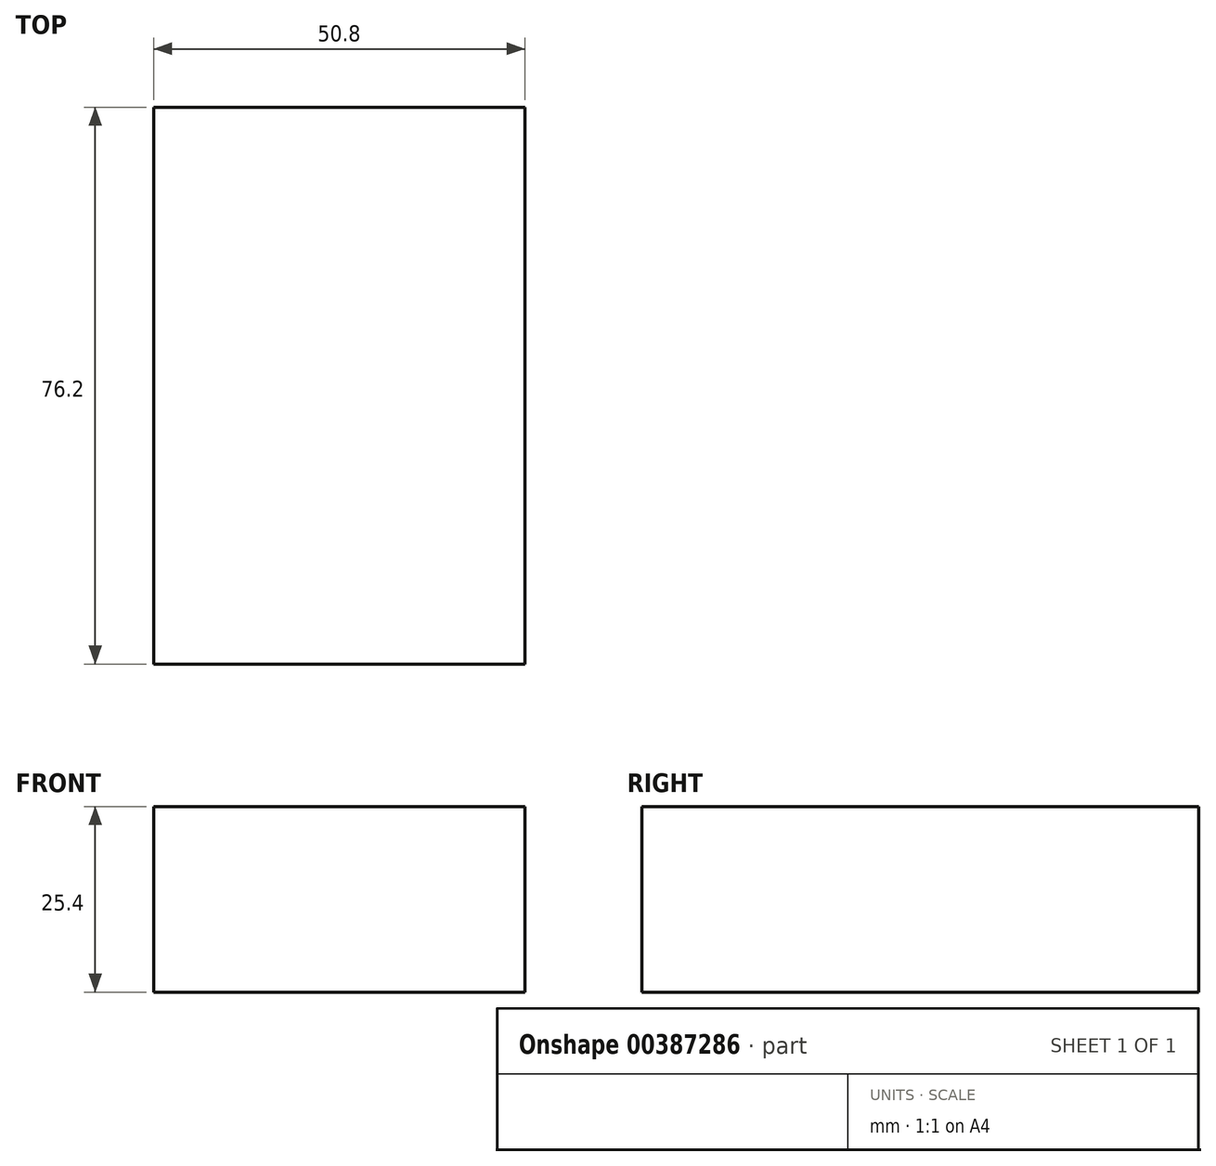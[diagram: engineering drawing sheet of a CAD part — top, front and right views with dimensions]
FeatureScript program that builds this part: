
annotation { "Feature Type Name" : "Feature", "Feature Type Description" : "" }
export const myFeature = defineFeature(function(context is Context, id is Id, definition is map)
    precondition{}
    {
        {
            var Q0;
            Q0=qCreatedBy(makeId("Top.planeOp"),FACE);
            var sketch = newSketch(context, id + "F0", { "sketchPlane" : qUnion([Q0])});
            skLineSegment(sketch, "E0.bottom", {"start": v(0, 0) * mm, "end": v(25.4, 0) * mm});
            skLineSegment(sketch, "E0.top", {"start": v(0, 25.4) * mm, "end": v(25.4, 25.4) * mm});
            skLineSegment(sketch, "E0.left", {"start": v(0, 0) * mm, "end": v(0, 25.4) * mm});
            skLineSegment(sketch, "E0.right", {"start": v(25.4, 0) * mm, "end": v(25.4, 25.4) * mm});
            skLineSegment(sketch, "E1.bottom", {"start": v(0, 0) * mm, "end": v(-25.4, 0) * mm});
            skLineSegment(sketch, "E1.top", {"start": v(0, 25.4) * mm, "end": v(-25.4, 25.4) * mm});
            skLineSegment(sketch, "E1.right", {"start": v(-25.4, 0) * mm, "end": v(-25.4, 25.4) * mm});
            skLineSegment(sketch, "E2.top", {"start": v(0, 50.8) * mm, "end": v(-25.4, 50.8) * mm});
            skLineSegment(sketch, "E2.left", {"start": v(0, 25.4) * mm, "end": v(0, 50.8) * mm});
            skLineSegment(sketch, "E2.right", {"start": v(-25.4, 25.4) * mm, "end": v(-25.4, 50.8) * mm});
            skLineSegment(sketch, "E3.top", {"start": v(0, 50.8) * mm, "end": v(25.4, 50.8) * mm});
            skLineSegment(sketch, "E3.right", {"start": v(25.4, 25.4) * mm, "end": v(25.4, 50.8) * mm});
            skLineSegment(sketch, "E4.top", {"start": v(0, 76.2) * mm, "end": v(25.4, 76.2) * mm});
            skLineSegment(sketch, "E4.left", {"start": v(0, 50.8) * mm, "end": v(0, 76.2) * mm});
            skLineSegment(sketch, "E4.right", {"start": v(25.4, 50.8) * mm, "end": v(25.4, 76.2) * mm});
            skLineSegment(sketch, "E5.top", {"start": v(0, 76.2) * mm, "end": v(-25.4, 76.2) * mm});
            skLineSegment(sketch, "E5.right", {"start": v(-25.4, 50.8) * mm, "end": v(-25.4, 76.2) * mm});
            skSolve(sketch);
        }
        {
            var Q0;
            Q0 = qSketchRegion(id + "F0", true);
            extrude(context, id + "F1", {"entities" : qUnion([Q0]), "depth" : 25.4 * mm});
        }
    });
